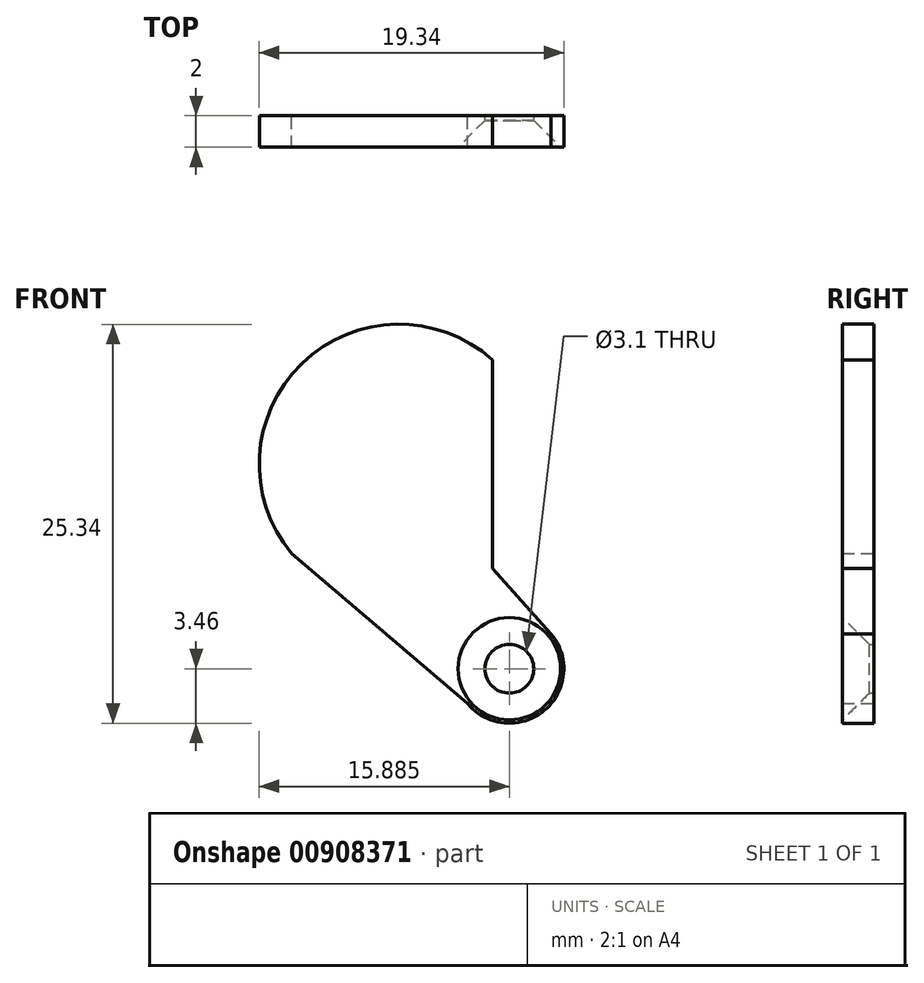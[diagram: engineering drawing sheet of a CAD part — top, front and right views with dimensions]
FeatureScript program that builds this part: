
annotation { "Feature Type Name" : "Feature", "Feature Type Description" : "" }
export const myFeature = defineFeature(function(context is Context, id is Id, definition is map)
    precondition{}
    {
        {
            var Q0;
            Q0=qCreatedBy(makeId("Front.planeOp"),FACE);
            var sketch = newSketch(context, id + "F0", { "sketchPlane" : qUnion([Q0])});
            skCircle(sketch, "E0", {"center": v(-3.43, -24) * mm, "radius": 8.88 * mm, "construction": true});
            skLineSegment(sketch, "E1", {"start": v(2.48, -17.38) * mm, "end": v(2.48, -30.62) * mm});
            skCircle(sketch, "E2", {"center": v(3.57, -37) * mm, "radius": 3.46 * mm, "construction": true});
            skLineSegment(sketch, "E3", {"start": v(0.9, -39.21) * mm, "end": v(6.22, -34.79) * mm, "construction": true});
            skLineSegment(sketch, "E4", {"start": v(6.22, -34.79) * mm, "end": v(2.48, -30.62) * mm});
            skLineSegment(sketch, "E5", {"start": v(-3.43, -24) * mm, "end": v(-10.26, -29.68) * mm, "construction": true});
            skLineSegment(sketch, "E6", {"start": v(0.9, -39.21) * mm, "end": v(-10.26, -29.68) * mm});
            skArc(sketch, "E7", {"start": v(-10.26, -29.68) * mm, "mid": v(-9.6, -17.61) * mm, "end": v(2.48, -17.38) * mm});
            skArc(sketch, "E8", {"start": v(0.9, -39.21) * mm, "mid": v(5.78, -39.66) * mm, "end": v(6.22, -34.79) * mm});
            skArc(sketch, "E9.MirrorCS", {"start": v(0.9, 39.21) * mm, "mid": v(5.78, 39.66) * mm, "end": v(6.22, 34.79) * mm});
            skArc(sketch, "E10.MirrorCS", {"start": v(-10.26, 29.68) * mm, "mid": v(-9.6, 17.61) * mm, "end": v(2.48, 17.38) * mm});
            skLineSegment(sketch, "E11.MirrorCS", {"start": v(0.9, 39.21) * mm, "end": v(-10.26, 29.68) * mm});
            skLineSegment(sketch, "E12.MirrorCS", {"start": v(0.9, 39.21) * mm, "end": v(6.22, 34.79) * mm, "construction": true});
            skCircle(sketch, "E13.MirrorC", {"center": v(-3.43, 24) * mm, "radius": 8.88 * mm, "construction": true});
            skCircle(sketch, "E14.MirrorC", {"center": v(3.57, 37) * mm, "radius": 3.46 * mm, "construction": true});
            skLineSegment(sketch, "E15.MirrorCS", {"start": v(2.48, 17.38) * mm, "end": v(2.48, 30.62) * mm});
            skLineSegment(sketch, "E16.MirrorCS", {"start": v(-3.43, 24) * mm, "end": v(-10.26, 29.68) * mm, "construction": true});
            skLineSegment(sketch, "E17.MirrorCS", {"start": v(6.22, 34.79) * mm, "end": v(2.48, 30.62) * mm});
            skCircle(sketch, "E18", {"center": v(3.57, -37) * mm, "radius": 1.55 * mm});
            skCircle(sketch, "E19", {"center": v(3.57, 37) * mm, "radius": 1.55 * mm});
            skSolve(sketch);
        }
        {
            var Q0;
            Q0=makeQuery(id+"F0.imprint","IMPRINT",FACE,{"disambiguationData":[TD([[makeQuery(id+"F0.imprint","IMPRINT",EDGE,{"derivedFrom":sQuery(id+"F0.wireOp",EDGE,"E1")}),-1.0]])]});
            var Q1;
            Q1=makeQuery(id+"F0.imprint","IMPRINT",FACE,{"disambiguationData":[TD([[makeQuery(id+"F0.imprint","IMPRINT",EDGE,{"derivedFrom":sQuery(id+"F0.wireOp",EDGE,"E9.MirrorCS")}),-1.0]])]});
            extrude(context, id + "F1", {"entities" : qUnion([Q0, Q1]), "depth" : 2 * mm, "offsetDistance" : 25 * mm});
        }
        {
            var Q0;
            Q0=makeQuery(id+"F1.opExtrude","CAP_EDGE",EDGE,{"disambiguationData":[OSD([sQuery(id+"F0.wireOp",EDGE,"E18")])],"isStart":false});
            var Q1;
            Q1=makeQuery(id+"F1.opExtrude","CAP_EDGE",EDGE,{"disambiguationData":[OSD([sQuery(id+"F0.wireOp",EDGE,"E19")])],"isStart":false});
            chamfer(context, id + "F2", {"entities" : qUnion([Q0, Q1]), "width" : 1.7 * mm, "tangentPropagation" : true});
        }
    });
